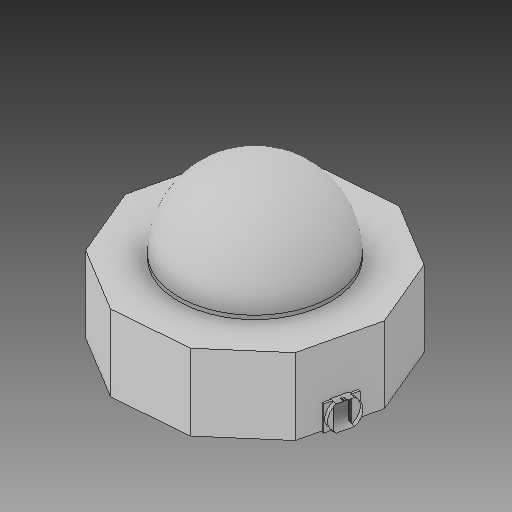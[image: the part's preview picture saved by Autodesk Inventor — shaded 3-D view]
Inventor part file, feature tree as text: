
AUTODESK INVENTOR PART (.ipt)
format: ipt  version: 2017 (Build 210142000, 142)  size: 280,064 bytes
history: native  units: in
note: dims shown in document units (in); Inventor stores cm internally (conversion verified against a paired STEP export)
features: sketch x7, extrude x6, other x3, mirror x1, delete_face x1
ambient origin geometry x8: Origin, YZ Plane, XZ Plane, XY Plane, X Axis, Y Axis, Z Axis, Center Point
bodies: Solid1 (feature_tree)
feature tree (18):
  other  "dome"
  extrude  "bace"  Depth=1.0in TaperAngle=0.0deg
  extrude  "bace wall"  Depth=20.0in TaperAngle=0.0deg
  extrude  "bace ceiling"  Depth=2.0in
  other  "dome work plane"
  extrude  "door frame"  Depth=0.25in
  extrude  "corridor connection"  Depth=2.0in
  extrude  "left door slot"  Depth=21.0in
  other  "door slot mirror"
  mirror  "Mirror1"
  delete_face  "Delete Face6"
  sketch  "Sketch1"  dims[d0=62.0in d1=1.0in d2=0.0in]
  sketch  "Sketch2"  dims[d4=1.0in d5=20.0in d6=0.0in]
  sketch  "Sketch3"  dims[d8=1.0in d9=0.0in d16=2.0in d17=6.6667in]
  sketch  "Sketch8"  dims[d18=1.0in d19=0.0in d22=0.25in d23=0.5in d24=6.6667in]
  sketch  "Sketch9"  dims[d25=2.0in d26=0.0in d28=40.0in]
  sketch  "Sketch10"  dims[d32=20.0in d33=21.0in]
  sketch  "Sketch12"  dims[d34=90.0deg d91=4.0in d92=0.5833in d93=3.8873in d94=3.8873in d95=1.7083in d96=0.0625in d97=0.0625in d98=1.6458in d99=0.25in d100=0.125in d101=0.0884in d102=45.0deg d103=3.3333in d104=1.0in d105=0.125in d106=1.0in d107=1.0in d108=0.0in]
